# Revit family: ASH_Contour21_S6363_BIM_GB
name_source: partatom
category: Plumbing Fixtures
revit_build: Autodesk Revit MEP 2012 (Build: 20110309_2315(x64)
units: mm (PartAtom-declared; Revit-internal decimal feet)

## types (4) — shared parameters
AccessibilityPerformance = DDA Compliant
Accessories = www.idealspec.co.uk
Assembly Code = C1030200
AssetType = Fixed
BIMObjectName = GRABRAIL_ArmitageShanks_Contour21-TRHolder_S6363AC
BREEAM Approved = No
Brand = ArmitageShanks
Category = Furniture_GRABRAIL_UK
CurrentRevision = 1
Default Elevation = 1219 mm
Description = Toilet roll holder for Contour 21 hinged arm rail
DurationUnit = Years
ECA = No
ExpectedLife = 30
Features = Not lockable
Help = http://www.idealspec.co.uk
InstallationInstructions = http://www.idealspec.co.uk
Manufacturer = Ideal Standard International Ltd
ManufacturerURL = www.idealspec.co.uk
Material = Plastic
Name = GRABRAIL_ArmitageShanks_Contour21-TRHolder_S6363AC
NettWeight = 0.34Kg
NominalLength = 97 mm
ProductDataSheet = http://www.idealspec.co.uk
ProductInformation = http://www.idealspec.co.uk
SalesInformation = http://www.idealspec.co.uk
SendEnquiry = http://www.idealspec.co.uk
Shape = Profiled
Size = mm x mm x mm
Space = Internal
SpareParts = www.fastpart-spares.co.uk
StandardsConformance = DDA, Doc-M
URL = www.idealspec.co.uk
Version = 1
VolumeUnits = Litres
WRAS = No
WarrantyDescription = Manufacturers Warranty
WarrantyDurationParts = 5
WarrantyDurationUnit = Years
WarrantyGuarantorParts = Ideal Standard International Ltd
WaterEfficientProduct = No
zero-valued in all types: NominalWidth, NominlHeight

## per-type parameters (varying)
| type | Color | Finish | TRHColour |
| S6363AC | White | White | Plastic White AC |
| S6363RN | Charcoal | Charcoal | Plastic Charcoal RN |
| S636336 | Blue | Blue | Plastic Blue 36 |
| S6363LJ | Light Grey | Light Grey | Plastic Light Grey LJ |

note: column(s) folded — value = type name in every type: Model, ModelNumber, ModelReference, PartNumber

## geometry (parser evidence)
native form markers: Blend x4, Sweep x3
no freeform markers — native parametric forms only
